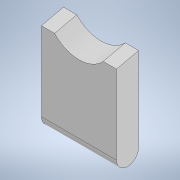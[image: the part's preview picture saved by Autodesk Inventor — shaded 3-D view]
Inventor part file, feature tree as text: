
AUTODESK INVENTOR PART (.ipt)
format: ipt  version: 2021 (Build 250183000, 183)  size: 128,000 bytes
history: native  units: mm
features: sketch x4, extrude x2, fillet x1, plane x1, sweep x1
ambient origin geometry x8: Origin, YZ Plane, XZ Plane, XY Plane, X Axis, Y Axis, Z Axis, Center Point
bodies: Solid1 (feature_tree)
feature tree (9):
  extrude  "Extrusion1"  Depth=21.5mm
  fillet  "Fillet2"  Radius=5.0mm
  plane  "Work Plane1"
  sweep  "Sweep1"
  extrude  "Extrusion6"  TaperAngle=0.0deg  [1 undecoded]
  sketch  "Sketch1"  dims[d0=17.0mm d1=21.5mm d2=5.0mm d3=0.0mm]
  sketch  "Sketch5"  dims[d15=2.5mm d21=-8.5mm]
  sketch  "Sketch6"  dims[d22=2.268928mm d25=0.0mm d26=0.0mm]
  sketch  "Sketch8"  dims[d27=3.0mm d31=3.0mm d32=3.0mm d33=3.0mm d34=7.5mm d35=17.0mm d36=0.0mm d16=0.872665mm d17=0.5mm d18=0.872665mm]
note: 1 required parameter value undecoded (feature->parameter linkage not recoverable at this tier; creation-order binding heuristic only, values carry confidence <= 0.55)
